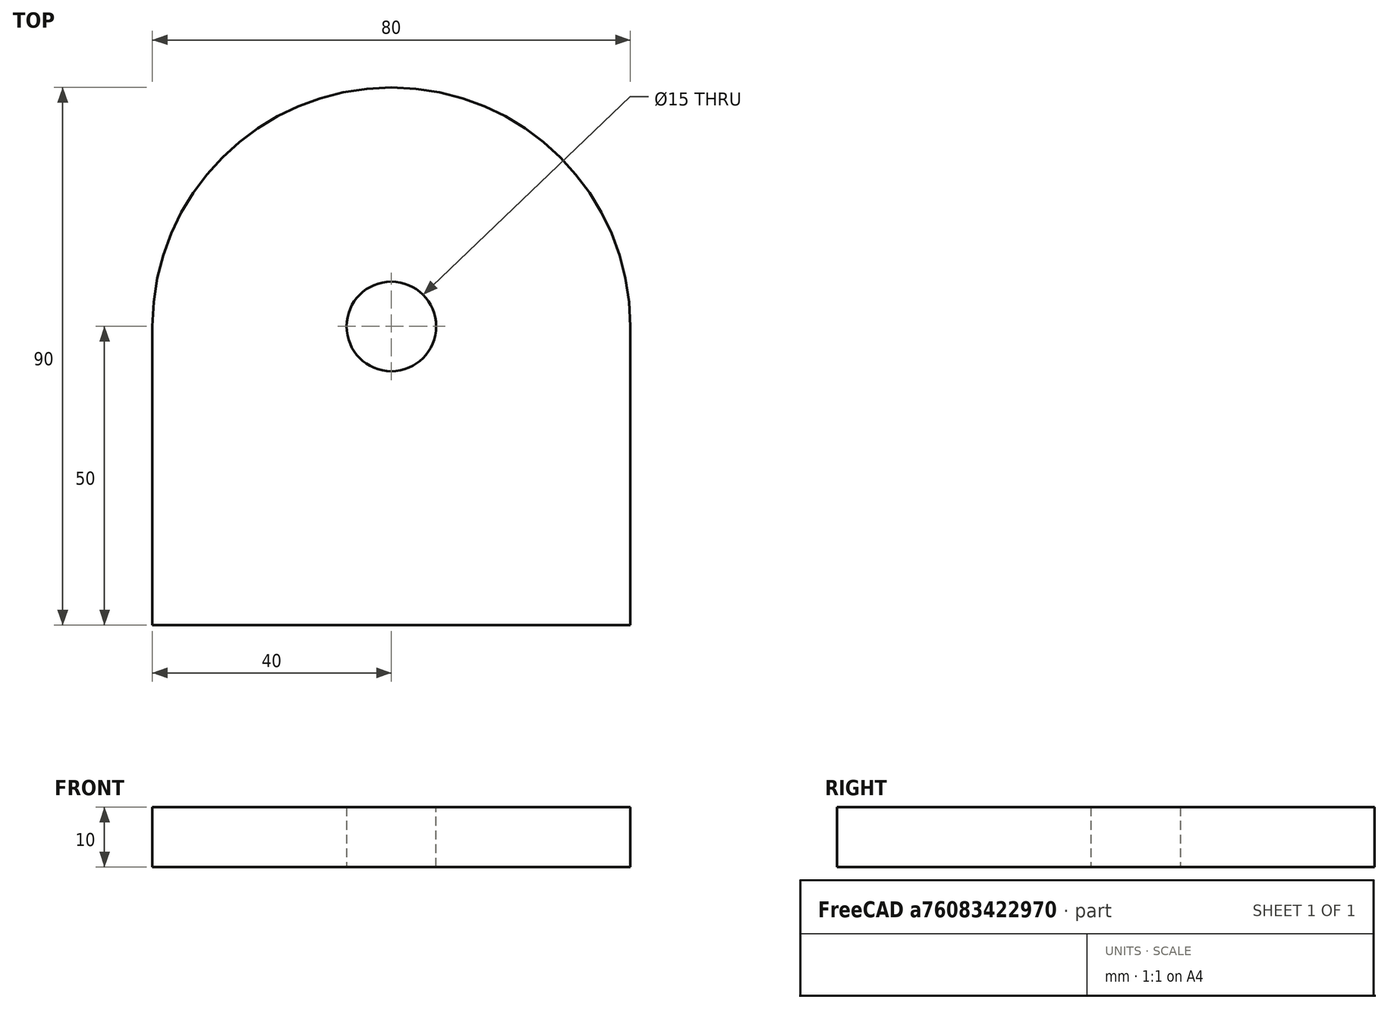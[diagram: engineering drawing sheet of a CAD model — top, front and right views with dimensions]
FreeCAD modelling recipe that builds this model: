
FCSTD DOCUMENT  (FreeCAD 0.18R4 (GitTag))
Label: armBase
License: All rights reserved
LicenseURL: http://en.wikipedia.org/wiki/All_rights_reserved
objects: Sketcher::SketchObject×1, PartDesign::Pad×1, PartDesign::Body×1, Part::Feature×1
note: 5 computed .brp shape members not serialized (recipe doc carries the construction recipe); baked Part::Feature solids carry a one-line shape summary decoded from their .brp

FEATURE [Sketcher::SketchObject] Sketch
  MapMode = 5
  Support = -> [XY_Plane]
  sketch-geometry (5):
    g0: LineSegment StartX=80 StartY=50 StartZ=0 EndX=80 EndY=0 EndZ=0
    g1: LineSegment StartX=80 StartY=0 StartZ=0 EndX=0 EndY=0 EndZ=0
    g2: LineSegment StartX=0 StartY=0 StartZ=0 EndX=0 EndY=50 EndZ=0
    g3: ArcOfCircle CenterX=40 CenterY=50 CenterZ=0 NormalX=0 NormalY=0 NormalZ=1 AngleXU=0 Radius=40 StartAngle=2.06649e-08 EndAngle=3.14159
    g4: Circle CenterX=40 CenterY=50 CenterZ=0 NormalX=0 NormalY=0 NormalZ=1 AngleXU=0 Radius=7.5
  constraints (14):
    c: Coincident(g0,g1)
    c: Coincident(g1,g2)
    c: Horizontal(g1)
    c: Vertical(g0)
    c: Vertical(g2)
    c: DistanceX(g2,g0) = 80
    c: DistanceY(g0,g0) = 50
    c: Coincident(g-1,g1)
    c: Radius(g3) = 40
    c: Coincident(g3,g2)
    c: Coincident(g3,g0)
    c: Diameter(g4) = 15
    c: Coincident(g3,g4)
    c: Horizontal(g2,g0)
FEATURE [PartDesign::Pad] Pad
  Length = 10
  Length2 = 100
  Profile = -> Sketch
  Type = 0
FEATURE [PartDesign::Body] Body
  Group = -> [Sketch,Pad]
  Origin = -> Origin
  Tip = -> Pad
FEATURE [Part::Feature] Pad001  label="Robot_ArmBase"
  shape: bbox 80 x 90 x 10 mm, 7 faces (baked)
